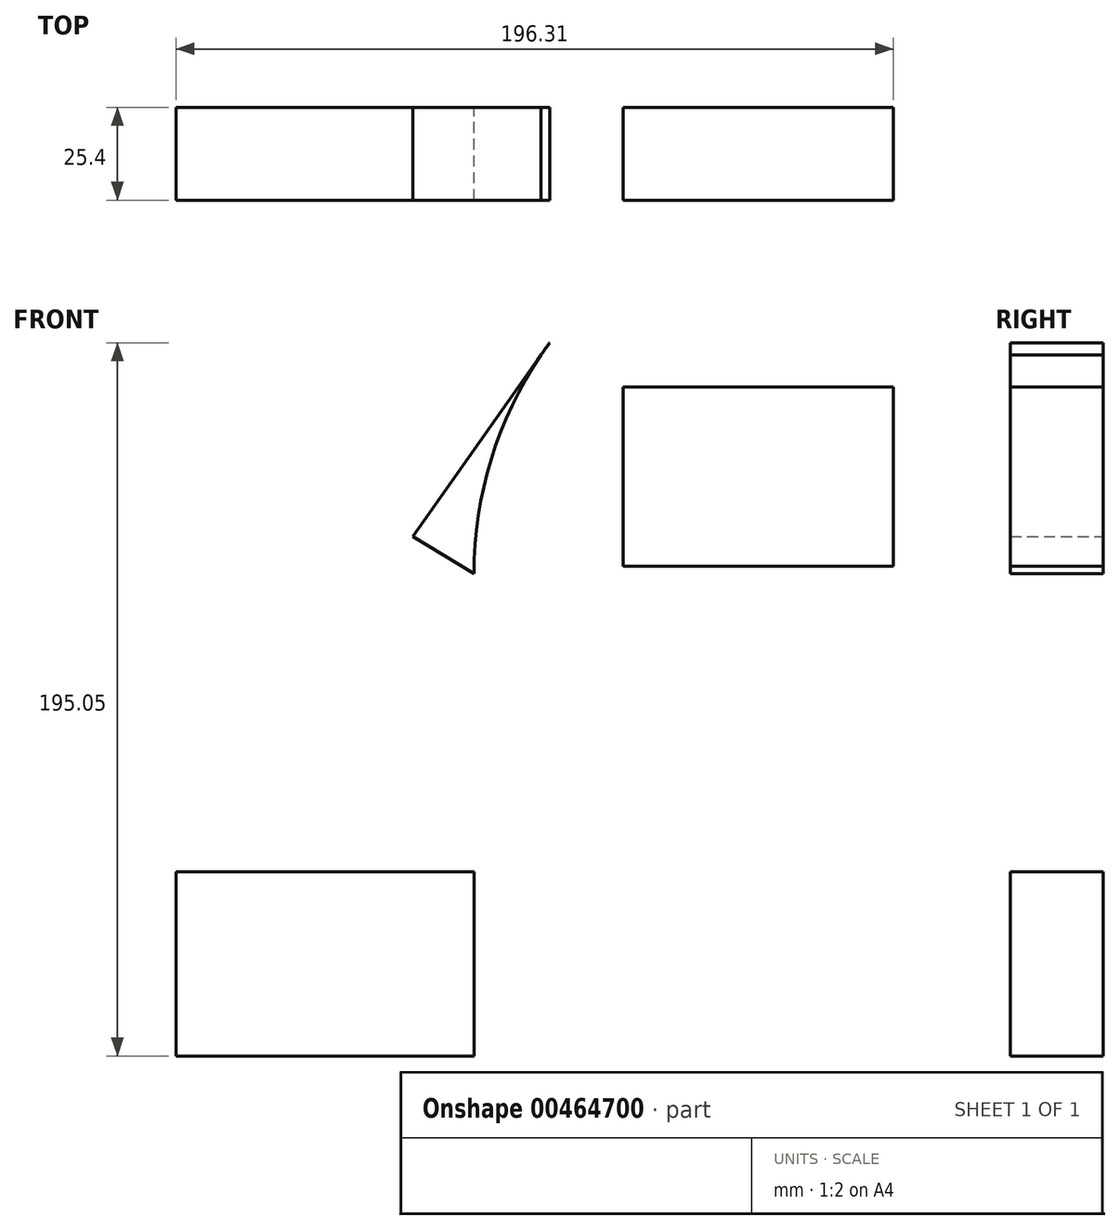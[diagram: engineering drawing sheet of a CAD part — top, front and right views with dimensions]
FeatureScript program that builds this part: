
annotation { "Feature Type Name" : "Feature", "Feature Type Description" : "" }
export const myFeature = defineFeature(function(context is Context, id is Id, definition is map)
    precondition{}
    {
        {
            var Q0;
            Q0=qCreatedBy(makeId("Front.planeOp"),FACE);
            var sketch = newSketch(context, id + "F0", { "sketchPlane" : qUnion([Q0])});
            skLineSegment(sketch, "E0.bottom", {"start": v(-40.77, 25.17) * mm, "end": v(40.77, 25.17) * mm});
            skLineSegment(sketch, "E0.top", {"start": v(-40.77, -25.17) * mm, "end": v(40.77, -25.17) * mm});
            skLineSegment(sketch, "E0.left", {"start": v(-40.77, 25.17) * mm, "end": v(-40.77, -25.17) * mm});
            skLineSegment(sketch, "E0.right", {"start": v(40.77, 25.17) * mm, "end": v(40.77, -25.17) * mm});
            skPoint(sketch, "E0.middle", {"position": v(0, 0) * mm});
            skLineSegment(sketch, "E1", {"start": v(40.77, 25.17) * mm, "end": v(40.77, 106.7) * mm});
            skLineSegment(sketch, "E2", {"start": v(-40.77, 30.42) * mm, "end": v(-40.77, 116.87) * mm});
            skLineSegment(sketch, "E3.bottom", {"start": v(155.54, 108.82) * mm, "end": v(81.53, 108.82) * mm});
            skLineSegment(sketch, "E3.top", {"start": v(155.54, 157.74) * mm, "end": v(81.53, 157.74) * mm});
            skLineSegment(sketch, "E3.left", {"start": v(155.54, 108.82) * mm, "end": v(155.54, 157.74) * mm});
            skLineSegment(sketch, "E3.right", {"start": v(81.53, 108.82) * mm, "end": v(81.53, 157.74) * mm});
            skPoint(sketch, "E3.middle", {"position": v(118.54, 133.28) * mm});
            skArc(sketch, "E4", {"start": v(40.77, 106.7) * mm, "mid": v(46.9, 142.38) * mm, "end": v(64.6, 173.95) * mm});
            skLineSegment(sketch, "E5", {"start": v(64.6, 173.95) * mm, "end": v(118.54, 133.28) * mm});
            skArc(sketch, "E6", {"start": v(-40.77, 116.87) * mm, "mid": v(-5.76, 174.45) * mm, "end": v(61.46, 169.88) * mm});
            skLineSegment(sketch, "E7", {"start": v(24.09, 116.87) * mm, "end": v(61.46, 169.88) * mm});
            skLineSegment(sketch, "E8", {"start": v(24.09, 116.87) * mm, "end": v(40.77, 106.7) * mm});
            skSolve(sketch);
        }
        {
            var Q0;
            Q0 = qSketchRegion(id + "F0", true);
            extrude(context, id + "F1", {"entities" : qUnion([Q0]), "depth" : 25.4 * mm});
        }
    });
